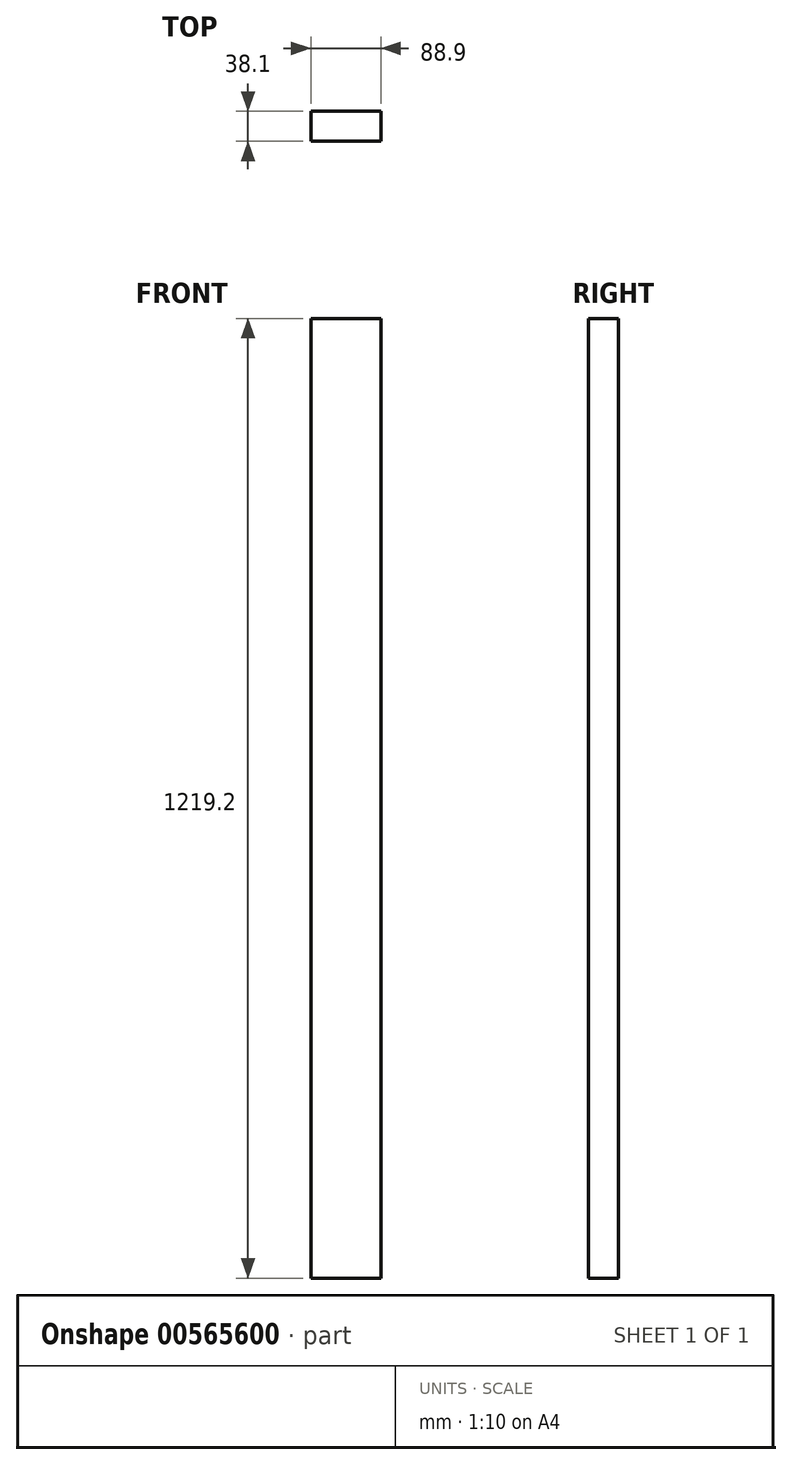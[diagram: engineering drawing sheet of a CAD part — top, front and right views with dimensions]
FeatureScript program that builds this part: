
annotation { "Feature Type Name" : "Feature", "Feature Type Description" : "" }
export const myFeature = defineFeature(function(context is Context, id is Id, definition is map)
    precondition{}
    {
        {
            var Q0;
            Q0=qCreatedBy(makeId("Top.planeOp"),FACE);
            var sketch = newSketch(context, id + "F0", { "sketchPlane" : qUnion([Q0])});
            skLineSegment(sketch, "E0.bottom", {"start": v(0, 0) * mm, "end": v(88.9, 0) * mm});
            skLineSegment(sketch, "E0.top", {"start": v(0, 38.1) * mm, "end": v(88.9, 38.1) * mm});
            skLineSegment(sketch, "E0.left", {"start": v(0, 0) * mm, "end": v(0, 38.1) * mm});
            skLineSegment(sketch, "E0.right", {"start": v(88.9, 0) * mm, "end": v(88.9, 38.1) * mm});
            skSolve(sketch);
        }
        {
            var Q0;
            Q0=qSketchRegion(id+"F0",true);
            extrude(context, id + "F1", {"entities" : qUnion([Q0]), "depth" : 1219.2 * mm, "offsetDistance" : 25.4 * mm});
        }
    });
